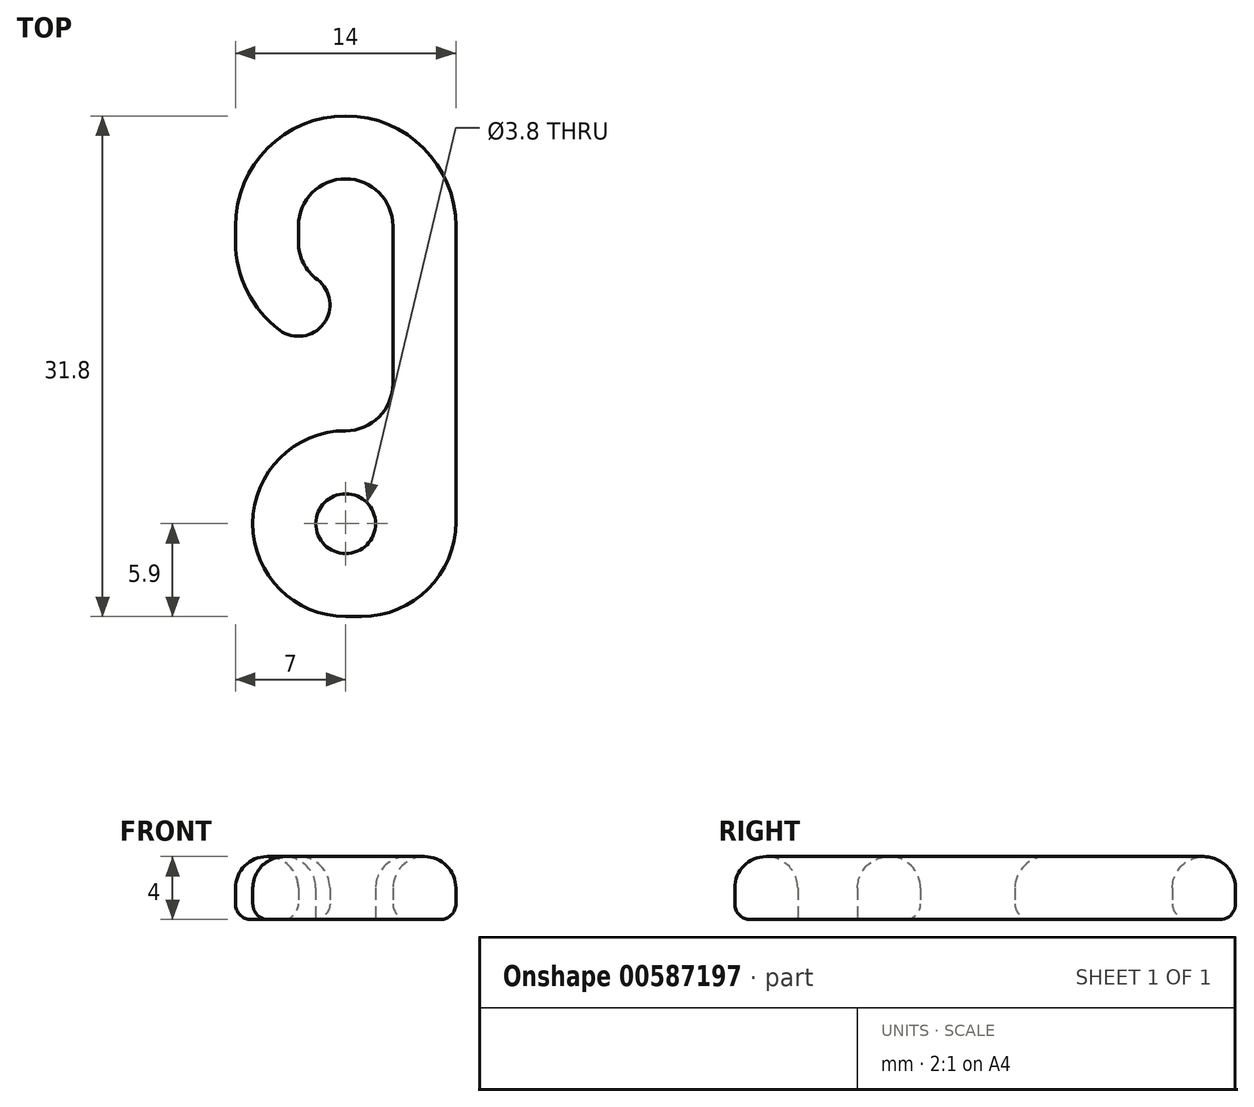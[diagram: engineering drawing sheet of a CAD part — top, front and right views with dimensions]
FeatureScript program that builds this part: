
annotation { "Feature Type Name" : "Feature", "Feature Type Description" : "" }
export const myFeature = defineFeature(function(context is Context, id is Id, definition is map)
    precondition{}
    {
        {
            var Q0;
            Q0=qCreatedBy(makeId("Top.planeOp"),FACE);
            var sketch = newSketch(context, id + "F0", { "sketchPlane" : qUnion([Q0])});
            skArc(sketch, "E0", {"start": v(3, 0) * mm, "mid": v(0, 3) * mm, "end": v(-3, 0) * mm});
            skArc(sketch, "E1", {"start": v(7, 0) * mm, "mid": v(0, 7) * mm, "end": v(-7, 0) * mm});
            skCircle(sketch, "E2", {"center": v(0, -18.9) * mm, "radius": 1.9 * mm});
            skArc(sketch, "E3", {"start": v(0, -13) * mm, "mid": v(-5.9, -18.9) * mm, "end": v(0, -24.8) * mm});
            skLineSegment(sketch, "E4", {"start": v(-5.9, -18.9) * mm, "end": v(5.9, -18.9) * mm, "construction": true});
            skLineSegment(sketch, "E5", {"start": v(-7, 0) * mm, "end": v(7, 0) * mm, "construction": true});
            skLineSegment(sketch, "E6", {"start": v(3, 0) * mm, "end": v(3, -12.4) * mm});
            skLineSegment(sketch, "E7", {"start": v(-1, -12.4) * mm, "end": v(-1, 0.67) * mm, "construction": true});
            skLineSegment(sketch, "E8", {"start": v(-3, 0) * mm, "end": v(-3, -1) * mm});
            skLineSegment(sketch, "E9", {"start": v(-7, 0) * mm, "end": v(-7, -1) * mm});
            skPoint(sketch, "E10.orphan", {"position": v(-1, -6.93) * mm});
            skPoint(sketch, "E11.end.orphan", {"position": v(-1, -2.83) * mm});
            skArc(sketch, "E12", {"start": v(-3, -1) * mm, "mid": v(-2.68, -2.34) * mm, "end": v(-1.8, -3.4) * mm});
            skArc(sketch, "E13", {"start": v(-7, -1) * mm, "mid": v(-6.26, -4.13) * mm, "end": v(-4.2, -6.6) * mm});
            skLineSegment(sketch, "E14", {"start": v(-1, -5) * mm, "end": v(-1, -5) * mm});
            skPoint(sketch, "E15.visualSharp", {"position": v(-1, -3.83) * mm});
            skArc(sketch, "E15.filletArc", {"start": v(-1, -5) * mm, "mid": v(-1.21, -4.1) * mm, "end": v(-1.8, -3.4) * mm});
            skPoint(sketch, "E16.visualSharp", {"position": v(-1, -7.93) * mm});
            skArc(sketch, "E16.filletArc", {"start": v(-4.2, -6.6) * mm, "mid": v(-2.1, -6.79) * mm, "end": v(-1, -5) * mm});
            skLineSegment(sketch, "E17", {"start": v(-12.48, -13) * mm, "end": v(10.64, -13) * mm, "construction": true});
            skArc(sketch, "E18", {"start": v(0, -13) * mm, "mid": v(2.12, -12.12) * mm, "end": v(3, -10) * mm});
            skLineSegment(sketch, "E19", {"start": v(7, 0) * mm, "end": v(7, -18.8) * mm});
            skLineSegment(sketch, "E20", {"start": v(0, -24.8) * mm, "end": v(1, -24.8) * mm});
            skArc(sketch, "E21.filletArc", {"start": v(1, -24.8) * mm, "mid": v(5.24, -23.04) * mm, "end": v(7, -18.8) * mm});
            skSolve(sketch);
        }
        {
            var Q0;
            {var subQ1=sQuery(id+"F0.wireOp",EDGE,"E0");Q0=makeQuery(id+"F0.imprint","IMPRINT",FACE,{"disambiguationData":[TD([[makeQuery(id+"F0.imprint","IMPRINT",EDGE,{"derivedFrom":subQ1}),-1.0]])]});}
            extrude(context, id + "F1", {"entities" : qUnion([Q0]), "depth" : 4 * mm, "offsetDistance" : 25 * mm});
        }
        {
            var Q0;
            Q0=makeQuery(id+"F1.opExtrude","CAP_EDGE",EDGE,{"disambiguationData":[OSD([sQuery(id+"F0.wireOp",EDGE,"E0")])],"isStart":false});
            var Q1;
            Q1=makeQuery(id+"F1.opExtrude","CAP_EDGE",EDGE,{"disambiguationData":[OSD([sQuery(id+"F0.wireOp",EDGE,"E2")])],"isStart":false});
            fillet(context, id + "F2", {"entities" : qUnion([Q0, Q1]), "radius" : 2 * mm, "tangentPropagation" : true, "allowEdgeOverflow" : false});
        }
        {
            var Q0;
            Q0=makeQuery(id+"F1.opExtrude","CAP_EDGE",EDGE,{"disambiguationData":[OSD([sQuery(id+"F0.wireOp",EDGE,"E19")])],"isStart":true});
            var Q1;
            Q1=makeQuery(id+"F1.opExtrude","CAP_EDGE",EDGE,{"disambiguationData":[OSD([sQuery(id+"F0.wireOp",EDGE,"E1")])],"isStart":true});
            var Q2;
            Q2=makeQuery(id+"F1.opExtrude","CAP_EDGE",EDGE,{"disambiguationData":[OSD([sQuery(id+"F0.wireOp",EDGE,"E9")])],"isStart":true});
            fillet(context, id + "F3", {"entities" : qUnion([Q0, Q1, Q2]), "radius" : 1 * mm, "tangentPropagation" : true, "allowEdgeOverflow" : false});
        }
    });
